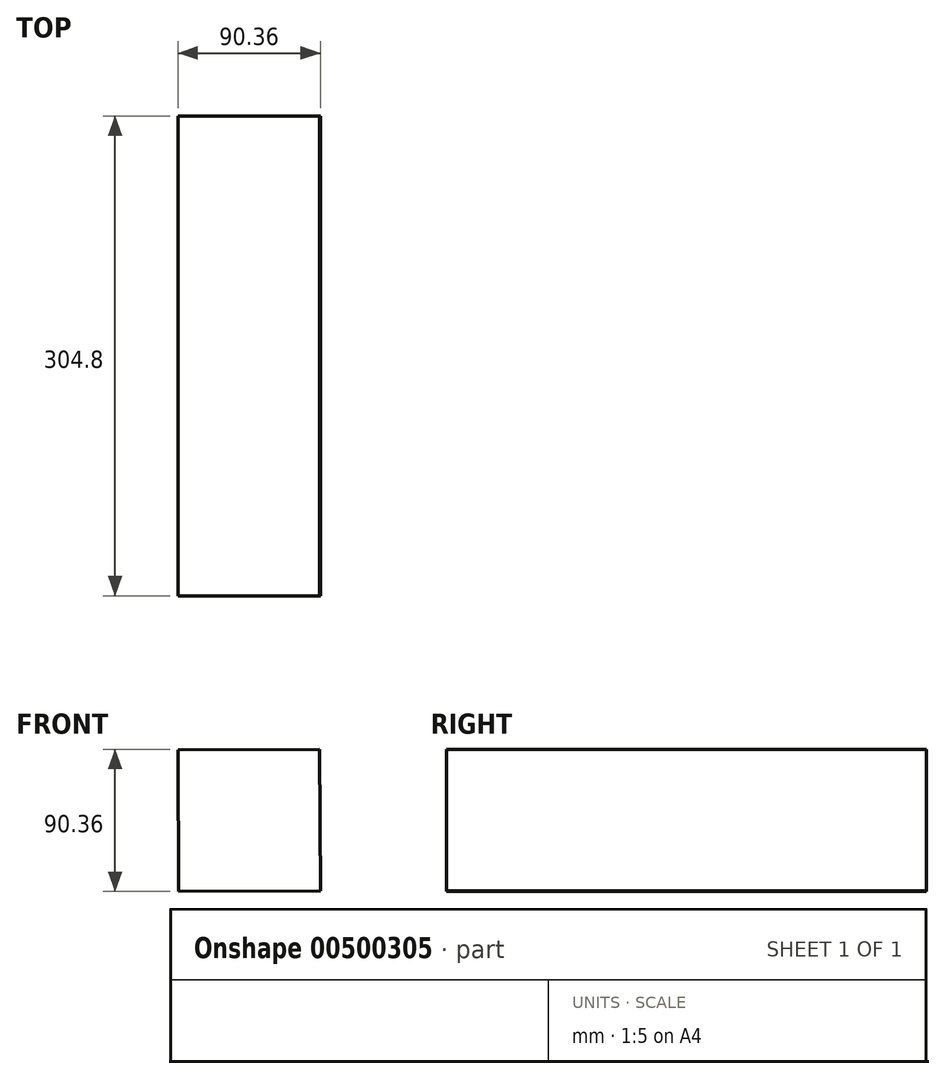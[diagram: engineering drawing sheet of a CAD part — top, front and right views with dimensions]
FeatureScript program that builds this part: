
annotation { "Feature Type Name" : "Feature", "Feature Type Description" : "" }
export const myFeature = defineFeature(function(context is Context, id is Id, definition is map)
    precondition{}
    {
        {
            var Q0;
            Q0=qCreatedBy(makeId("Front.planeOp"),FACE);
            var sketch = newSketch(context, id + "F0", { "sketchPlane" : qUnion([Q0])});
            skCircle(sketch, "E0.cCircle", {"center": v(0, 0) * mm, "radius": 63.58 * mm, "construction": true});
            skLineSegment(sketch, "E0.0", {"start": v(-45.18, 44.74) * mm, "end": v(44.74, 45.18) * mm});
            skLineSegment(sketch, "E0.1", {"start": v(44.74, 45.18) * mm, "end": v(45.18, -44.74) * mm});
            skLineSegment(sketch, "E0.2", {"start": v(45.18, -44.74) * mm, "end": v(-44.74, -45.18) * mm});
            skLineSegment(sketch, "E0.3", {"start": v(-44.74, -45.18) * mm, "end": v(-45.18, 44.74) * mm});
            skSolve(sketch);
        }
        {
            var Q0;
            Q0=makeQuery(id+"F0.imprint","IMPRINT",FACE,{"disambiguationData":[TD([[makeQuery(id+"F0.imprint","IMPRINT",EDGE,{"derivedFrom":sQuery(id+"F0.wireOp",EDGE,"E0.0")}),-1.0]])]});
            extrude(context, id + "F1", {"entities" : qUnion([Q0]), "depth" : 304.8 * mm});
        }
    });
